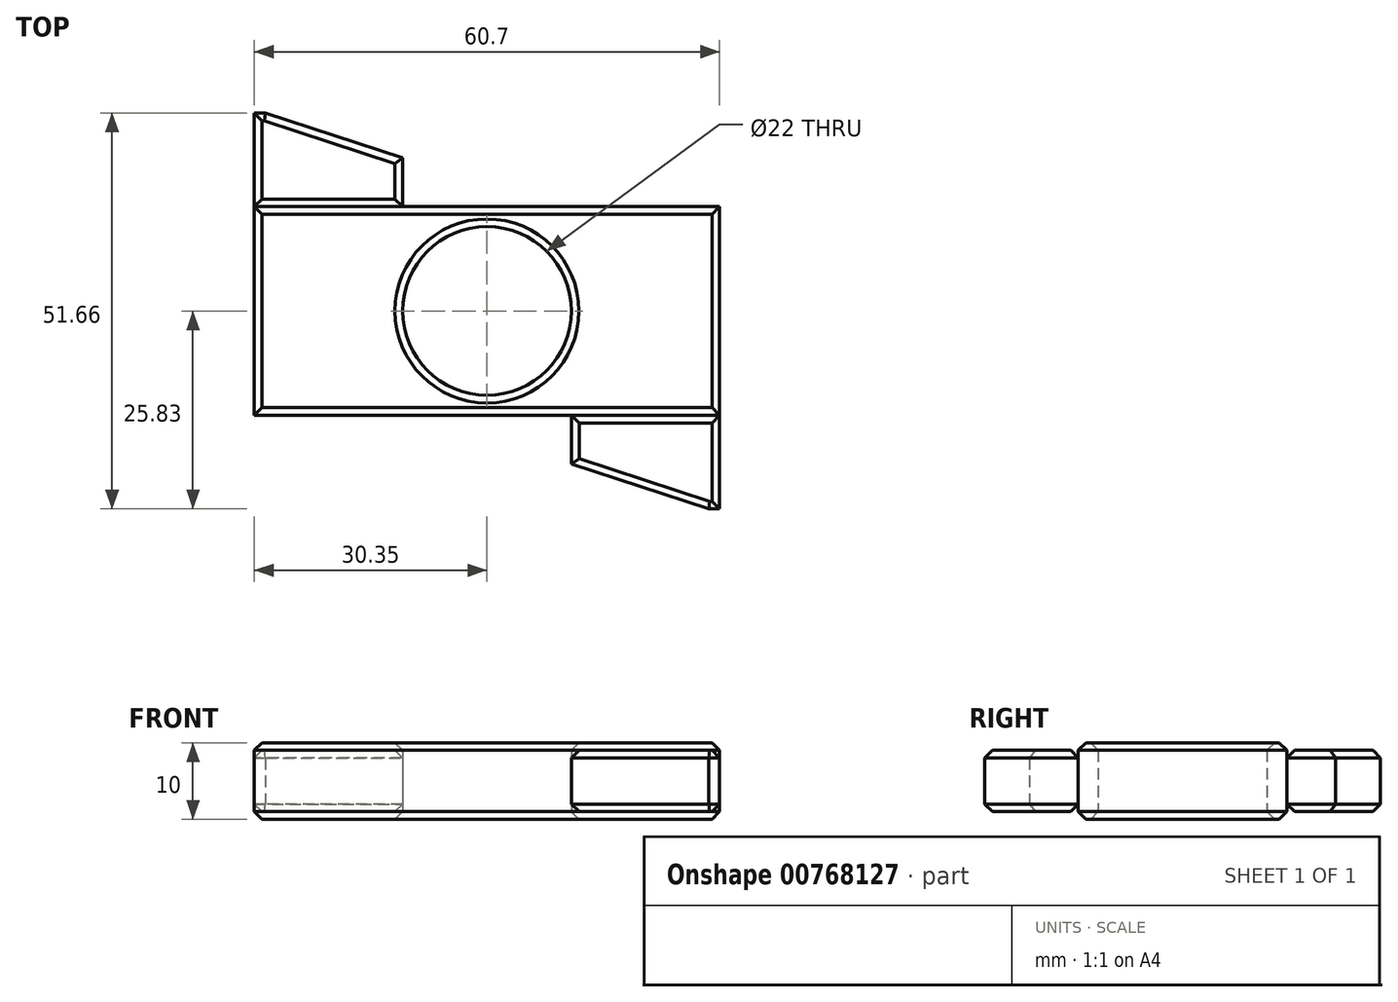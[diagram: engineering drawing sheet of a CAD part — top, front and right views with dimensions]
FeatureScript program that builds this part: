
annotation { "Feature Type Name" : "Feature", "Feature Type Description" : "" }
export const myFeature = defineFeature(function(context is Context, id is Id, definition is map)
    precondition{}
    {
        {
            var Q0;
            Q0=qCreatedBy(makeId("Top.planeOp"),FACE);
            var sketch = newSketch(context, id + "F0", { "sketchPlane" : qUnion([Q0])});
            skLineSegment(sketch, "E0.bottom", {"start": v(30.35, -13.6) * mm, "end": v(-30.35, -13.6) * mm});
            skLineSegment(sketch, "E0.top", {"start": v(30.35, 13.6) * mm, "end": v(-30.35, 13.6) * mm});
            skLineSegment(sketch, "E0.left", {"start": v(30.35, -13.6) * mm, "end": v(30.35, 13.6) * mm});
            skLineSegment(sketch, "E0.right", {"start": v(-30.35, -13.6) * mm, "end": v(-30.35, 13.6) * mm});
            skPoint(sketch, "E0.middle", {"position": v(0, 0) * mm});
            skCircle(sketch, "E1", {"center": v(0, 0) * mm, "radius": 11 * mm});
            skLineSegment(sketch, "E2", {"start": v(30.35, -13.6) * mm, "end": v(30.35, -25.83) * mm});
            skLineSegment(sketch, "E3", {"start": v(28.9, -25.83) * mm, "end": v(11.03, -19.97) * mm});
            skLineSegment(sketch, "E4", {"start": v(11.03, -19.97) * mm, "end": v(11.03, -13.6) * mm});
            skLineSegment(sketch, "E5.MirrorCS", {"start": v(-30.35, 13.6) * mm, "end": v(-30.35, 25.83) * mm});
            skLineSegment(sketch, "E6.MirrorCS", {"start": v(-28.9, 25.83) * mm, "end": v(-11.03, 19.97) * mm});
            skLineSegment(sketch, "E7.MirrorCS", {"start": v(-11.03, 19.97) * mm, "end": v(-11.03, 13.6) * mm});
            skLineSegment(sketch, "E8", {"start": v(-30.35, 25.83) * mm, "end": v(-28.9, 25.83) * mm});
            skLineSegment(sketch, "E9", {"start": v(28.9, -25.83) * mm, "end": v(30.35, -25.83) * mm});
            skSolve(sketch);
        }
        {
            var Q0;
            {var subQ1=sQuery(id+"F0.wireOp",EDGE,"E2");Q0=makeQuery(id+"F0.imprint","IMPRINT",FACE,{"disambiguationData":[TD([[makeQuery(id+"F0.imprint","IMPRINT",EDGE,{"derivedFrom":subQ1}),-1.0]])]});}
            var Q1;
            {var subQ1=sQuery(id+"F0.wireOp",EDGE,"E5.MirrorCS");Q1=makeQuery(id+"F0.imprint","IMPRINT",FACE,{"disambiguationData":[TD([[makeQuery(id+"F0.imprint","IMPRINT",EDGE,{"derivedFrom":subQ1}),-1.0]])]});}
            extrude(context, id + "F1", {"entities" : qUnion([Q0, Q1]), "endBound" : BoundingType.SYMMETRIC, "depth" : 8 * mm, "offsetDistance" : 25 * mm});
        }
        {
            var Q0;
            {var subQ3=sQuery(id+"F0.wireOp",EDGE,"E0.left");Q0=makeQuery(id+"F0.imprint","IMPRINT",FACE,{"disambiguationData":[TD([[makeQuery(id+"F0.imprint","IMPRINT",EDGE,{"derivedFrom":subQ3}),1.0]])]});}
            extrude(context, id + "F2", {"entities" : qUnion([Q0]), "endBound" : BoundingType.SYMMETRIC, "depth" : 10 * mm, "offsetDistance" : 25 * mm});
        }
        {
            var Q0;
            Q0=makeQuery(id+"F2.opExtrude","CAP_FACE",FACE,{"disambiguationData":[OSD([sQuery(id+"F0.wireOp",EDGE,"E0.bottom"),sQuery(id+"F0.wireOp",EDGE,"E0.top"),sQuery(id+"F0.wireOp",EDGE,"E0.left"),sQuery(id+"F0.wireOp",EDGE,"E0.right"),sQuery(id+"F0.wireOp",EDGE,"E1")])],"isStart":false});
            var Q1;
            Q1=makeQuery(id+"F2.opExtrude","CAP_FACE",FACE,{"disambiguationData":[OSD([sQuery(id+"F0.wireOp",EDGE,"E0.bottom"),sQuery(id+"F0.wireOp",EDGE,"E0.top"),sQuery(id+"F0.wireOp",EDGE,"E0.left"),sQuery(id+"F0.wireOp",EDGE,"E0.right"),sQuery(id+"F0.wireOp",EDGE,"E1")])],"isStart":true});
            var Q2;
            Q2=makeQuery(id+"F1.opExtrude","CAP_FACE",FACE,{"disambiguationData":[OSD([sQuery(id+"F0.wireOp",EDGE,"E0.bottom"),sQuery(id+"F0.wireOp",EDGE,"E2"),sQuery(id+"F0.wireOp",EDGE,"E3"),sQuery(id+"F0.wireOp",EDGE,"E4"),sQuery(id+"F0.wireOp",EDGE,"E9")])],"isStart":true});
            var Q3;
            Q3=makeQuery(id+"F1.opExtrude","CAP_FACE",FACE,{"disambiguationData":[OSD([sQuery(id+"F0.wireOp",EDGE,"E0.top"),sQuery(id+"F0.wireOp",EDGE,"E5.MirrorCS"),sQuery(id+"F0.wireOp",EDGE,"E6.MirrorCS"),sQuery(id+"F0.wireOp",EDGE,"E7.MirrorCS"),sQuery(id+"F0.wireOp",EDGE,"E8")])],"isStart":true});
            var Q4;
            Q4=makeQuery(id+"F1.opExtrude","CAP_FACE",FACE,{"disambiguationData":[OSD([sQuery(id+"F0.wireOp",EDGE,"E0.top"),sQuery(id+"F0.wireOp",EDGE,"E5.MirrorCS"),sQuery(id+"F0.wireOp",EDGE,"E6.MirrorCS"),sQuery(id+"F0.wireOp",EDGE,"E7.MirrorCS"),sQuery(id+"F0.wireOp",EDGE,"E8")])],"isStart":false});
            var Q5;
            Q5=makeQuery(id+"F1.opExtrude","CAP_FACE",FACE,{"disambiguationData":[OSD([sQuery(id+"F0.wireOp",EDGE,"E0.bottom"),sQuery(id+"F0.wireOp",EDGE,"E2"),sQuery(id+"F0.wireOp",EDGE,"E3"),sQuery(id+"F0.wireOp",EDGE,"E4"),sQuery(id+"F0.wireOp",EDGE,"E9")])],"isStart":false});
            chamfer(context, id + "F3", {"entities" : qUnion([Q0, Q1, Q2, Q3, Q4, Q5]), "width" : 1 * mm, "tangentPropagation" : true});
        }
    });
